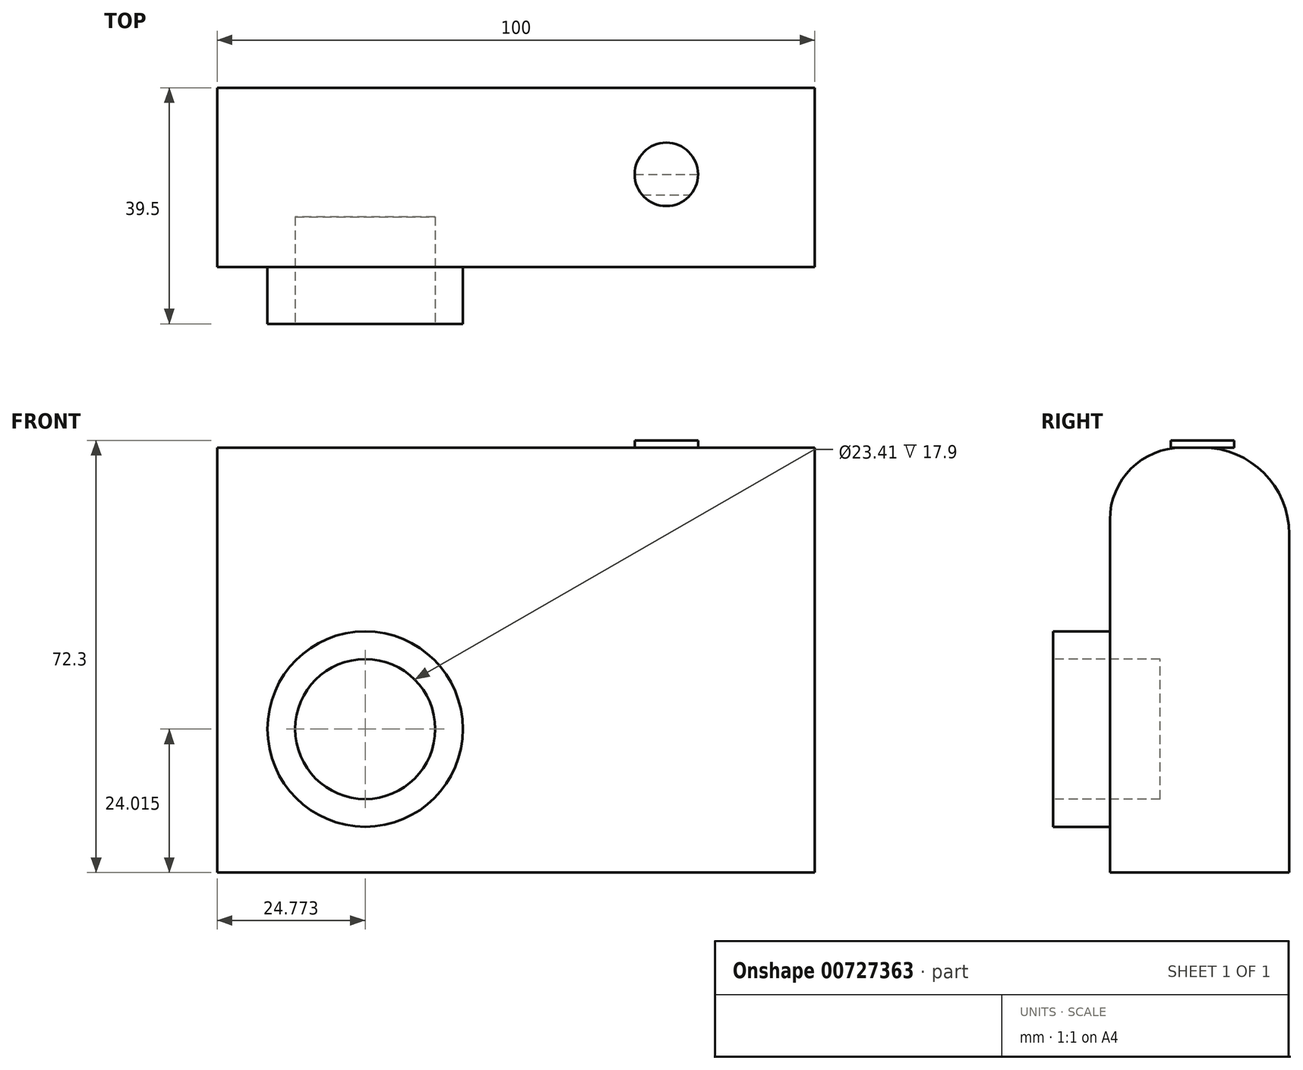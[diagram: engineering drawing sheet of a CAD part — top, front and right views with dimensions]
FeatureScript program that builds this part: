
annotation { "Feature Type Name" : "Feature", "Feature Type Description" : "" }
export const myFeature = defineFeature(function(context is Context, id is Id, definition is map)
    precondition{}
    {
        {
            var Q0;
            Q0=qCreatedBy(makeId("Top.planeOp"),FACE);
            var sketch = newSketch(context, id + "F0", { "sketchPlane" : qUnion([Q0])});
            skLineSegment(sketch, "E0.bottom", {"start": v(-73.75, 1.43) * mm, "end": v(26.25, 1.43) * mm});
            skLineSegment(sketch, "E0.top", {"start": v(-73.75, -28.57) * mm, "end": v(26.25, -28.57) * mm});
            skLineSegment(sketch, "E0.left", {"start": v(-73.75, 1.43) * mm, "end": v(-73.75, -28.57) * mm});
            skLineSegment(sketch, "E0.right", {"start": v(26.25, 1.43) * mm, "end": v(26.25, -28.57) * mm});
            skSolve(sketch);
        }
        {
            var Q0;
            Q0 = qSketchRegion(id + "F0", true);
            extrude(context, id + "F1", {"entities" : qUnion([Q0]), "depth" : 71.1 * mm, "offsetDistance" : 25 * mm});
        }
        {
            var Q0;
            Q0=makeQuery(id+"F1.opExtrude","CAP_EDGE",EDGE,{"disambiguationData":[OSD([sQuery(id+"F0.wireOp",EDGE,"E0.top")])],"isStart":false});
            fillet(context, id + "F2", {"entities" : qUnion([Q0]), "radius" : 12.07 * mm, "tangentPropagation" : true, "allowEdgeOverflow" : false});
        }
        {
            var Q0;
            Q0=makeQuery(id+"F1.opExtrude","CAP_EDGE",EDGE,{"disambiguationData":[OSD([sQuery(id+"F0.wireOp",EDGE,"E0.bottom")])],"isStart":false});
            fillet(context, id + "F3", {"entities" : qUnion([Q0]), "radius" : 14.5 * mm, "tangentPropagation" : true, "allowEdgeOverflow" : false});
        }
        {
            var Q0;
            Q0=makeQuery(id+"F1.opExtrude","SWEPT_FACE",FACE,{"disambiguationData":[OSD([sQuery(id+"F0.wireOp",EDGE,"E0.top")])]});
            var sketch = newSketch(context, id + "F4", { "sketchPlane" : qUnion([Q0])});
            skCircle(sketch, "E1", {"center": v(-48.98, 24.01) * mm, "radius": 16.34 * mm});
            skSolve(sketch);
        }
        {
            var Q0;
            Q0=makeQuery(id+"F4.imprint","IMPRINT",FACE,{"disambiguationData":[TD([[makeQuery(id+"F4.imprint","IMPRINT",EDGE,{"derivedFrom":sQuery(id+"F4.wireOp",EDGE,"E1")}),1.0]])]});
            extrude(context, id + "F5", {"entities" : qUnion([Q0]), "operationType" : NewBodyOperationType.ADD, "depth" : 14.5 * mm, "offsetDistance" : 25 * mm});
        }
        {
            var Q0;
            Q0=makeQuery(id+"F5.opExtrude","CAP_FACE",FACE,{"disambiguationData":[OSD([sQuery(id+"F4.wireOp",EDGE,"E1")])],"isStart":false});
            var sketch = newSketch(context, id + "F6", { "sketchPlane" : qUnion([Q0])});
            skCircle(sketch, "E2", {"center": v(-48.98, 24.01) * mm, "radius": 11.18 * mm});
            skSolve(sketch);
        }
        {
            var Q0;
            Q0=makeQuery(id+"F6.imprint","IMPRINT",FACE,{"disambiguationData":[TD([[makeQuery(id+"F6.imprint","IMPRINT",EDGE,{"derivedFrom":sQuery(id+"F6.wireOp",EDGE,"E2")}),1.0]])]});
            extrude(context, id + "F7", {"entities" : qUnion([Q0]), "operationType" : NewBodyOperationType.ADD, "oppositeDirection" : true, "depth" : 5.8 * mm, "offsetDistance" : 25 * mm});
        }
        {
            var Q0;
            Q0=makeQuery(id+"F5.opExtrude","CAP_FACE",FACE,{"disambiguationData":[OSD([sQuery(id+"F4.wireOp",EDGE,"E1")])],"isStart":false});
            var sketch = newSketch(context, id + "F8", { "sketchPlane" : qUnion([Q0])});
            skCircle(sketch, "E3", {"center": v(-48.98, 24.01) * mm, "radius": 11.7 * mm});
            skSolve(sketch);
        }
        {
            var Q0;
            Q0=makeQuery(id+"F8.imprint","IMPRINT",FACE,{"disambiguationData":[TD([[makeQuery(id+"F8.imprint","IMPRINT",EDGE,{"derivedFrom":sQuery(id+"F8.wireOp",EDGE,"E3")}),1.0]])]});
            extrude(context, id + "F9", {"entities" : qUnion([Q0]), "operationType" : NewBodyOperationType.ADD, "depth" : 7.2 * mm, "offsetDistance" : 25 * mm});
        }
        {
            var Q0;
            Q0=makeQuery(id+"F9.opExtrude","CAP_FACE",FACE,{"disambiguationData":[OSD([sQuery(id+"F8.wireOp",EDGE,"E3")])],"isStart":false});
            extrude(context, id + "F10", {"entities" : qUnion([Q0]), "operationType" : NewBodyOperationType.REMOVE, "oppositeDirection" : true, "depth" : 30.1 * mm, "offsetDistance" : 25 * mm});
        }
        {
            var Q0;
            Q0=makeQuery(id+"F1.opExtrude","SWEPT_FACE",FACE,{"disambiguationData":[OSD([sQuery(id+"F0.wireOp",EDGE,"E0.top")])]});
            extrude(context, id + "F11", {"entities" : qUnion([Q0]), "operationType" : NewBodyOperationType.ADD, "depth" : 25 * mm, "offsetDistance" : 25 * mm});
        }
        {
            var Q0;
            Q0=makeQuery(id+"F11.opExtrude","CAP_FACE",FACE,{"disambiguationData":[OSD([sQuery(id+"F0.wireOp",EDGE,"E0.top")])],"isStart":false});
            extrude(context, id + "F12", {"entities" : qUnion([Q0]), "operationType" : NewBodyOperationType.REMOVE, "oppositeDirection" : true, "depth" : 25 * mm, "offsetDistance" : 25 * mm});
        }
        {
            var Q0;
            Q0=makeQuery(id+"F5.opExtrude","CAP_FACE",FACE,{"disambiguationData":[OSD([sQuery(id+"F4.wireOp",EDGE,"E1")])],"isStart":false});
            extrude(context, id + "F13", {"entities" : qUnion([Q0]), "operationType" : NewBodyOperationType.REMOVE, "oppositeDirection" : true, "depth" : 5 * mm, "offsetDistance" : 25 * mm});
        }
        {
            var Q0;
            Q0=makeQuery(id+"F1.opExtrude","CAP_FACE",FACE,{"disambiguationData":[OSD([sQuery(id+"F0.wireOp",EDGE,"E0.bottom"),sQuery(id+"F0.wireOp",EDGE,"E0.top"),sQuery(id+"F0.wireOp",EDGE,"E0.left"),sQuery(id+"F0.wireOp",EDGE,"E0.right")])],"isStart":false});
            var sketch = newSketch(context, id + "F14", { "sketchPlane" : qUnion([Q0])});
            skCircle(sketch, "E4", {"center": v(1.4, -13.06) * mm, "radius": 5.3 * mm});
            skSolve(sketch);
        }
        {
            var Q0;
            {var subQ0=sQuery(id+"F14.wireOp",EDGE,"E4");var subQ1=sQuery(id+"F0.wireOp",EDGE,"E0.bottom");var subQ2=makeQuery(id+"F3.opFillet","BLEND_EDGE",EDGE,{"blendedFrom":[makeQuery(id+"F1.opExtrude","CAP_EDGE",EDGE,{"disambiguationData":[OSD([subQ1])],"isStart":false}),makeQuery(id+"F1.opExtrude","CAP_FACE",FACE,{"disambiguationData":[OSD([subQ1,sQuery(id+"F0.wireOp",EDGE,"E0.top"),sQuery(id+"F0.wireOp",EDGE,"E0.left"),sQuery(id+"F0.wireOp",EDGE,"E0.right")])],"isStart":false})],"blendedInto":[makeQuery(id+"F1.opExtrude","CAP_FACE",FACE,{"disambiguationData":[OSD([subQ1,sQuery(id+"F0.wireOp",EDGE,"E0.top"),sQuery(id+"F0.wireOp",EDGE,"E0.left"),sQuery(id+"F0.wireOp",EDGE,"E0.right")])],"isStart":false})]});var subQ3=makeQuery(id+"F14.imprint","INTERSECT",VERTEX,{"disambiguationData":[OD(0.0)],"derivedFrom":[subQ2,subQ0]});Q0=makeQuery(id+"F14.imprint","IMPRINT",FACE,{"disambiguationData":[TD([[makeQuery(id+"F14.imprint","IMPRINT",EDGE,{"disambiguationData":[TD([[subQ3,1.0]])],"derivedFrom":subQ0}),1.0]])]});}
            var Q1;
            {var subQ0=sQuery(id+"F14.wireOp",EDGE,"E4");var subQ1=sQuery(id+"F0.wireOp",EDGE,"E0.top");var subQ2=sQuery(id+"F0.wireOp",EDGE,"E0.bottom");var subQ3=makeQuery(id+"F1.opExtrude","CAP_FACE",FACE,{"disambiguationData":[OSD([subQ2,subQ1,sQuery(id+"F0.wireOp",EDGE,"E0.left"),sQuery(id+"F0.wireOp",EDGE,"E0.right")])],"isStart":false});var subQ4=makeQuery(id+"F3.opFillet","BLEND_EDGE",EDGE,{"blendedFrom":[makeQuery(id+"F1.opExtrude","CAP_EDGE",EDGE,{"disambiguationData":[OSD([subQ2])],"isStart":false}),subQ3],"blendedInto":[subQ3]});var subQ5=makeQuery(id+"F14.imprint","INTERSECT",VERTEX,{"disambiguationData":[OD(0.0)],"derivedFrom":[subQ4,subQ0]});Q1=makeQuery(id+"F14.imprint","IMPRINT",FACE,{"disambiguationData":[TD([[makeQuery(id+"F14.imprint","IMPRINT",EDGE,{"disambiguationData":[TD([[subQ5,-1.0]])],"derivedFrom":subQ0}),1.0]])]});}
            var Q2;
            {var subQ0=sQuery(id+"F14.wireOp",EDGE,"E4");var subQ1=sQuery(id+"F0.wireOp",EDGE,"E0.top");var subQ2=makeQuery(id+"F2.opFillet","BLEND_EDGE",EDGE,{"blendedFrom":[makeQuery(id+"F1.opExtrude","CAP_EDGE",EDGE,{"disambiguationData":[OSD([subQ1])],"isStart":false}),makeQuery(id+"F1.opExtrude","CAP_FACE",FACE,{"disambiguationData":[OSD([sQuery(id+"F0.wireOp",EDGE,"E0.bottom"),subQ1,sQuery(id+"F0.wireOp",EDGE,"E0.left"),sQuery(id+"F0.wireOp",EDGE,"E0.right")])],"isStart":false})],"blendedInto":[makeQuery(id+"F1.opExtrude","CAP_FACE",FACE,{"disambiguationData":[OSD([sQuery(id+"F0.wireOp",EDGE,"E0.bottom"),subQ1,sQuery(id+"F0.wireOp",EDGE,"E0.left"),sQuery(id+"F0.wireOp",EDGE,"E0.right")])],"isStart":false})]});var subQ3=makeQuery(id+"F14.imprint","INTERSECT",VERTEX,{"disambiguationData":[OD(0.0)],"derivedFrom":[subQ2,subQ0]});Q2=makeQuery(id+"F14.imprint","IMPRINT",FACE,{"disambiguationData":[TD([[makeQuery(id+"F14.imprint","IMPRINT",EDGE,{"disambiguationData":[TD([[subQ3,-1.0]])],"derivedFrom":subQ0}),1.0]])]});}
            extrude(context, id + "F15", {"entities" : qUnion([Q0, Q1, Q2]), "operationType" : NewBodyOperationType.ADD, "depth" : 1.2 * mm, "offsetDistance" : 25 * mm});
        }
    });
